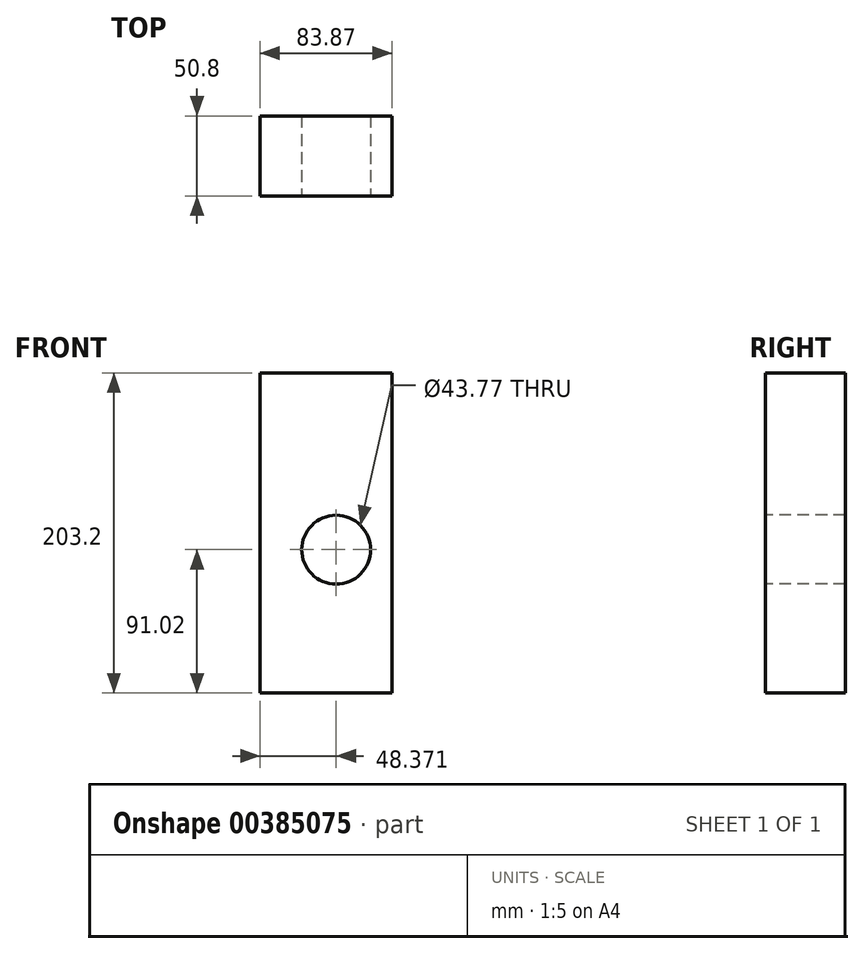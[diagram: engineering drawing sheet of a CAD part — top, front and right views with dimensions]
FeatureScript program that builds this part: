
annotation { "Feature Type Name" : "Feature", "Feature Type Description" : "" }
export const myFeature = defineFeature(function(context is Context, id is Id, definition is map)
    precondition{}
    {
        {
            var Q0;
            Q0=qCreatedBy(makeId("Right.planeOp"),FACE);
            var sketch = newSketch(context, id + "F0", { "sketchPlane" : qUnion([Q0])});
            skLineSegment(sketch, "E0.bottom", {"start": v(-44.45, -91.02) * mm, "end": v(-95.25, -91.02) * mm});
            skLineSegment(sketch, "E0.top", {"start": v(-44.45, 112.18) * mm, "end": v(-95.25, 112.18) * mm});
            skLineSegment(sketch, "E0.left", {"start": v(-44.45, -91.02) * mm, "end": v(-44.45, 112.18) * mm});
            skLineSegment(sketch, "E0.right", {"start": v(-95.25, -91.02) * mm, "end": v(-95.25, 112.18) * mm});
            skSolve(sketch);
        }
        {
            var Q0;
            Q0=makeQuery(id+"F0.imprint","IMPRINT",FACE,{"disambiguationData":[TD([[makeQuery(id+"F0.imprint","IMPRINT",EDGE,{"derivedFrom":sQuery(id+"F0.wireOp",EDGE,"E0.bottom")}),-1.0]])]});
            extrude(context, id + "F1", {"entities" : qUnion([Q0]), "depth" : 83.87 * mm});
        }
        {
            var Q0;
            Q0=makeQuery(id+"F1.opExtrude","SWEPT_FACE",FACE,{"disambiguationData":[OSD([sQuery(id+"F0.wireOp",EDGE,"E0.right")])]});
            var sketch = newSketch(context, id + "F2", { "sketchPlane" : qUnion([Q0])});
            skCircle(sketch, "E1", {"center": v(48.37, 0) * mm, "radius": 21.89 * mm});
            skSolve(sketch);
        }
        {
            var Q0;
            Q0=makeQuery(id+"F2.imprint","IMPRINT",FACE,{"disambiguationData":[TD([[makeQuery(id+"F2.imprint","IMPRINT",EDGE,{"derivedFrom":sQuery(id+"F2.wireOp",EDGE,"E1")}),1.0]])]});
            extrude(context, id + "F3", {"entities" : qUnion([Q0]), "operationType" : NewBodyOperationType.REMOVE, "endBound" : BoundingType.THROUGH_ALL, "oppositeDirection" : true, "depth" : 25.4 * mm});
        }
    });
